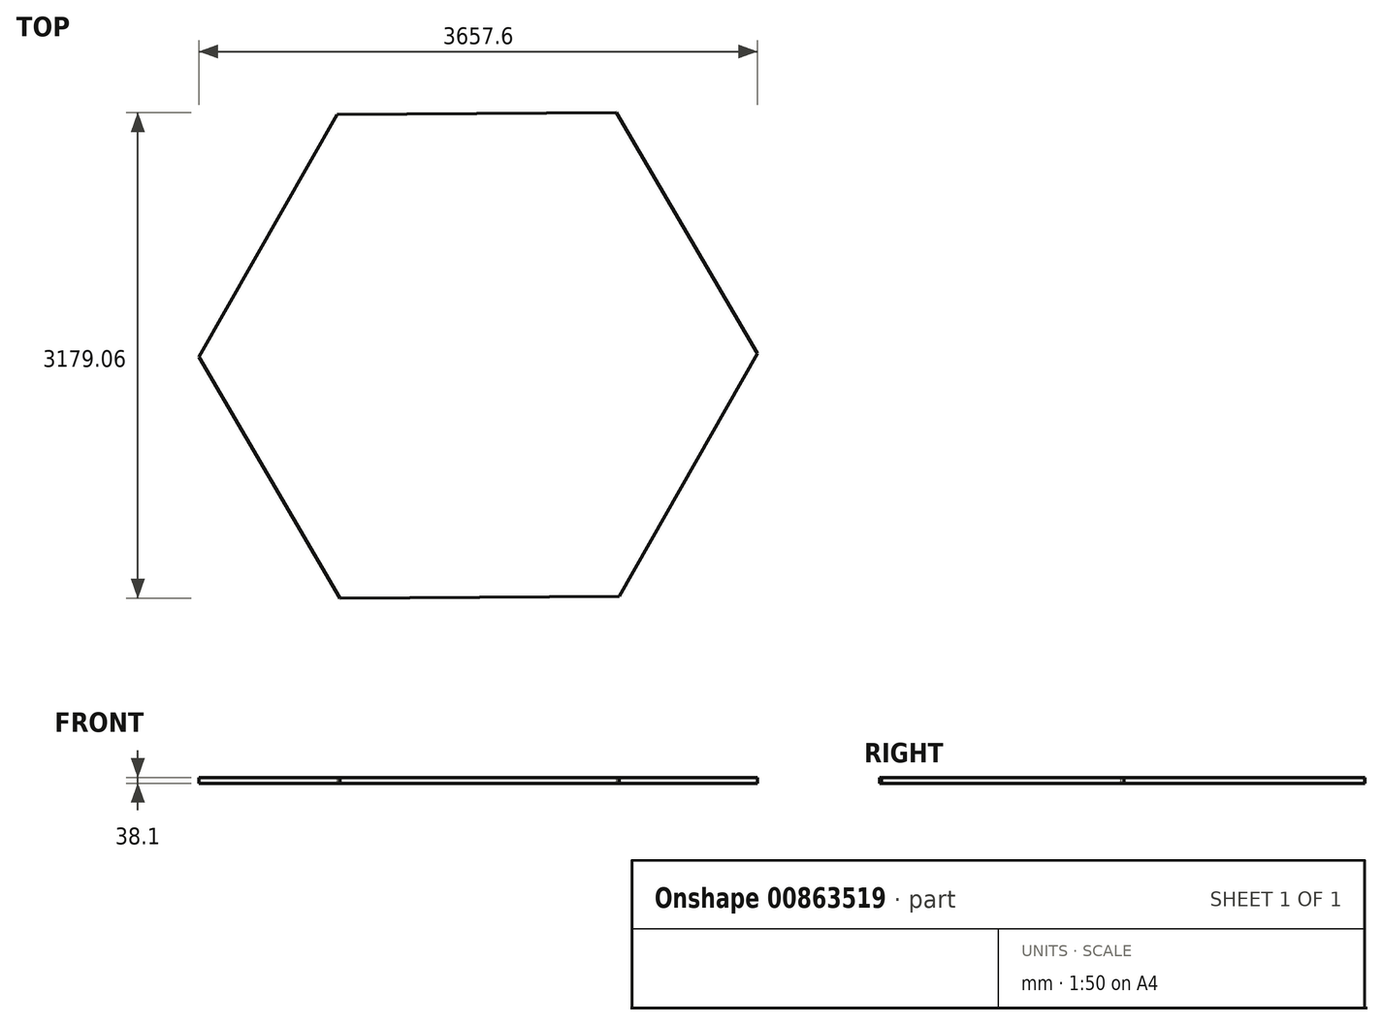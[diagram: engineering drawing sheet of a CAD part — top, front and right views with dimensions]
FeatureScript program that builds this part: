
annotation { "Feature Type Name" : "Feature", "Feature Type Description" : "" }
export const myFeature = defineFeature(function(context is Context, id is Id, definition is map)
    precondition{}
    {
        {
            var Q0;
            Q0=qCreatedBy(makeId("Top.planeOp"),FACE);
            var sketch = newSketch(context, id + "F0", { "sketchPlane" : qUnion([Q0])});
            skCircle(sketch, "E0.cCircle", {"center": v(0, 0) * mm, "radius": 1583.82 * mm, "construction": true});
            skLineSegment(sketch, "E0.0", {"start": v(904.45, 1589.53) * mm, "end": v(1828.8, 11.5) * mm});
            skLineSegment(sketch, "E0.1", {"start": v(1828.8, 11.5) * mm, "end": v(924.35, -1578.04) * mm});
            skLineSegment(sketch, "E0.2", {"start": v(924.35, -1578.04) * mm, "end": v(-904.45, -1589.53) * mm});
            skLineSegment(sketch, "E0.3", {"start": v(-904.45, -1589.53) * mm, "end": v(-1828.8, -11.5) * mm});
            skLineSegment(sketch, "E0.4", {"start": v(-1828.8, -11.5) * mm, "end": v(-924.35, 1578.04) * mm});
            skLineSegment(sketch, "E0.5", {"start": v(-924.35, 1578.04) * mm, "end": v(904.45, 1589.53) * mm});
            skPoint(sketch, "E0.0.midPoint", {"position": v(1366.62, 800.51) * mm});
            skSolve(sketch);
        }
        {
            var Q0;
            Q0 = qSketchRegion(id + "F0", true);
            extrude(context, id + "F1", {"entities" : qUnion([Q0]), "depth" : 38.1 * mm, "offsetDistance" : 25.4 * mm});
        }
    });
